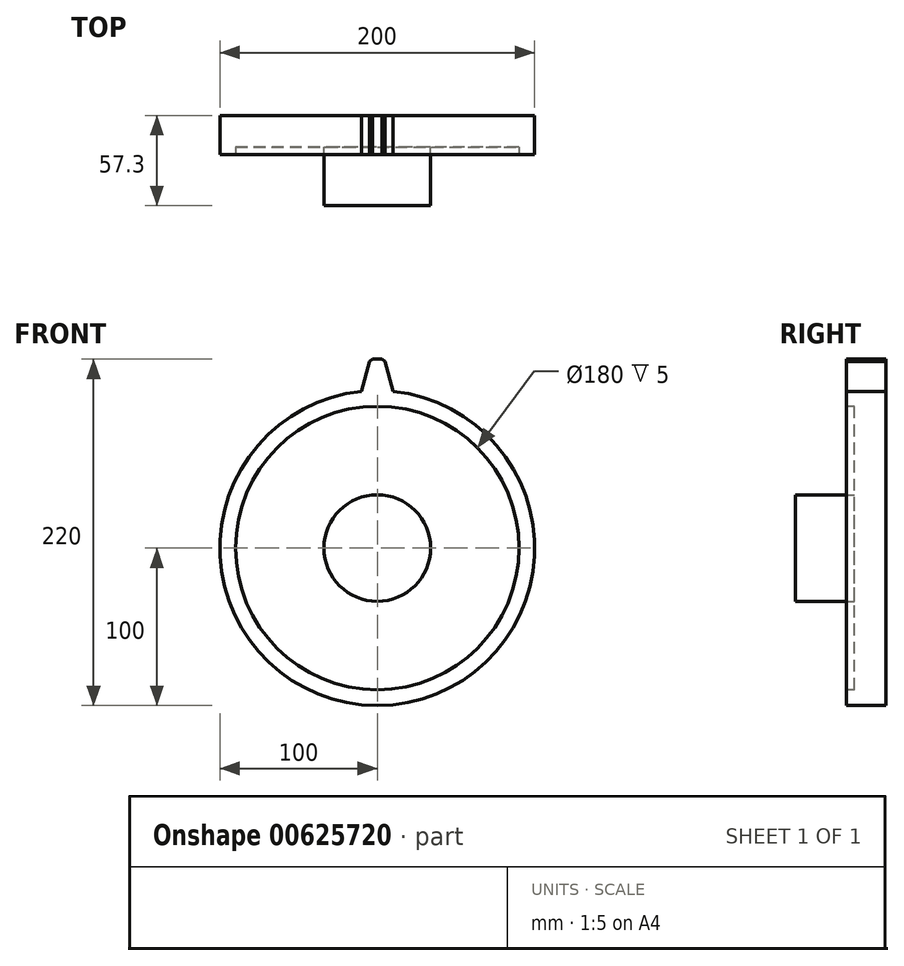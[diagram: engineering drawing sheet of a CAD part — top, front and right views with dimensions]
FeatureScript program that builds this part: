
annotation { "Feature Type Name" : "Feature", "Feature Type Description" : "" }
export const myFeature = defineFeature(function(context is Context, id is Id, definition is map)
    precondition{}
    {
        {
            var Q0;
            Q0=qCreatedBy(makeId("Front.planeOp"),FACE);
            var sketch = newSketch(context, id + "F0", { "sketchPlane" : qUnion([Q0])});
            skCircle(sketch, "E0", {"center": v(0, 0) * mm, "radius": 100 * mm});
            skSolve(sketch);
        }
        {
            var Q0;
            Q0 = qSketchRegion(id + "F0", true);
            extrude(context, id + "F1", {"entities" : qUnion([Q0]), "depth" : 25 * mm, "offsetDistance" : 25 * mm});
        }
        {
            var Q0;
            Q0=qCreatedBy(makeId("Front.planeOp"),FACE);
            var sketch = newSketch(context, id + "F2", { "sketchPlane" : qUnion([Q0])});
            skLineSegment(sketch, "E1", {"start": v(-10, 99.5) * mm, "end": v(10, 99.5) * mm});
            skLineSegment(sketch, "E2", {"start": v(10, 99.5) * mm, "end": v(4.5, 120) * mm});
            skLineSegment(sketch, "E3", {"start": v(4.5, 120) * mm, "end": v(-4.5, 120) * mm});
            skLineSegment(sketch, "E4", {"start": v(-4.5, 120) * mm, "end": v(-10, 99.5) * mm});
            skSolve(sketch);
        }
        {
            var Q0;
            Q0 = qSketchRegion(id + "F2", true);
            extrude(context, id + "F3", {"entities" : qUnion([Q0]), "operationType" : NewBodyOperationType.ADD, "depth" : 25 * mm, "offsetDistance" : 25 * mm});
        }
        {
            var Q0;
            Q0=makeQuery(id+"F3.opExtrude","SWEPT_EDGE",EDGE,{"disambiguationData":[OSD([sQuery(id+"F2.wireOp",EDGE,"E2"),sQuery(id+"F2.wireOp",EDGE,"E3")])]});
            var Q1;
            Q1=makeQuery(id+"F3.opExtrude","SWEPT_EDGE",EDGE,{"disambiguationData":[OSD([sQuery(id+"F2.wireOp",EDGE,"E3"),sQuery(id+"F2.wireOp",EDGE,"E4")])]});
            chamfer(context, id + "F4", {"entities" : qUnion([Q0, Q1]), "width" : 2 * mm, "tangentPropagation" : true});
        }
        {
            var Q0;
            Q0=makeQuery(id+"F3.opExtrude","SWEPT_EDGE",EDGE,{"disambiguationData":[OSD([sQuery(id+"F2.wireOp",EDGE,"E1"),sQuery(id+"F2.wireOp",EDGE,"E4")])]});
            var Q1;
            Q1=makeQuery(id+"F3.opExtrude","SWEPT_EDGE",EDGE,{"disambiguationData":[OSD([sQuery(id+"F2.wireOp",EDGE,"E1"),sQuery(id+"F2.wireOp",EDGE,"E2")])]});
            fillet(context, id + "F5", {"entities" : qUnion([Q0, Q1]), "radius" : 5 * mm, "tangentPropagation" : true, "allowEdgeOverflow" : false});
        }
        {
            var Q0;
            {var subQ0=sQuery(id+"F2.wireOp",EDGE,"E4");var subQ1=sQuery(id+"F2.wireOp",EDGE,"E3");var subQ2=sQuery(id+"F2.wireOp",EDGE,"E2");var subQ3=sQuery(id+"F2.wireOp",EDGE,"E1");Q0=makeQuery(id+"FSANccO2QEkQk0R_1.19.F3.boolean.opBoolean","MERGE",FACE,{"derivedFrom":[makeQuery(id+"FSANccO2QEkQk0R_1.18.F3.boolean.opBoolean","MERGE",FACE,{"derivedFrom":[makeQuery(id+"FSANccO2QEkQk0R_1.17.F3.boolean.opBoolean","MERGE",FACE,{"derivedFrom":[makeQuery(id+"FSANccO2QEkQk0R_1.16.F3.boolean.opBoolean","MERGE",FACE,{"derivedFrom":[makeQuery(id+"FSANccO2QEkQk0R_1.15.F3.boolean.opBoolean","MERGE",FACE,{"derivedFrom":[makeQuery(id+"FSANccO2QEkQk0R_1.14.F3.boolean.opBoolean","MERGE",FACE,{"derivedFrom":[makeQuery(id+"FSANccO2QEkQk0R_1.13.F3.boolean.opBoolean","MERGE",FACE,{"derivedFrom":[makeQuery(id+"FSANccO2QEkQk0R_1.12.F3.boolean.opBoolean","MERGE",FACE,{"derivedFrom":[makeQuery(id+"FSANccO2QEkQk0R_1.11.F3.boolean.opBoolean","MERGE",FACE,{"derivedFrom":[makeQuery(id+"FSANccO2QEkQk0R_1.10.F3.boolean.opBoolean","MERGE",FACE,{"derivedFrom":[makeQuery(id+"FSANccO2QEkQk0R_1.9.F3.boolean.opBoolean","MERGE",FACE,{"derivedFrom":[makeQuery(id+"FSANccO2QEkQk0R_1.8.F3.boolean.opBoolean","MERGE",FACE,{"derivedFrom":[makeQuery(id+"FSANccO2QEkQk0R_1.7.F3.boolean.opBoolean","MERGE",FACE,{"derivedFrom":[makeQuery(id+"FSANccO2QEkQk0R_1.6.F3.boolean.opBoolean","MERGE",FACE,{"derivedFrom":[makeQuery(id+"FSANccO2QEkQk0R_1.5.F3.boolean.opBoolean","MERGE",FACE,{"derivedFrom":[makeQuery(id+"FSANccO2QEkQk0R_1.4.F3.boolean.opBoolean","MERGE",FACE,{"derivedFrom":[makeQuery(id+"FSANccO2QEkQk0R_1.3.F3.boolean.opBoolean","MERGE",FACE,{"derivedFrom":[makeQuery(id+"FSANccO2QEkQk0R_1.2.F3.boolean.opBoolean","MERGE",FACE,{"derivedFrom":[makeQuery(id+"FSANccO2QEkQk0R_1.1.F3.boolean.opBoolean","MERGE",FACE,{"derivedFrom":[makeQuery(id+"F3.boolean.opBoolean","MERGE",FACE,{"derivedFrom":[makeQuery(id+"F1.opExtrude","CAP_FACE",FACE,{"disambiguationData":[OSD([sQuery(id+"F0.wireOp",EDGE,"E0")])],"isStart":false}),makeQuery(id+"F3.opExtrude","CAP_FACE",FACE,{"disambiguationData":[OSD([subQ3,subQ2,subQ1,subQ0])],"isStart":false})]}),makeQuery(id+"FSANccO2QEkQk0R_1.1.F3.opExtrude","CAP_FACE",FACE,{"disambiguationData":[OSD([subQ3,subQ2,subQ1,subQ0])],"isStart":false})]}),makeQuery(id+"FSANccO2QEkQk0R_1.2.F3.opExtrude","CAP_FACE",FACE,{"disambiguationData":[OSD([subQ3,subQ2,subQ1,subQ0])],"isStart":false})]}),makeQuery(id+"FSANccO2QEkQk0R_1.3.F3.opExtrude","CAP_FACE",FACE,{"disambiguationData":[OSD([subQ3,subQ2,subQ1,subQ0])],"isStart":false})]}),makeQuery(id+"FSANccO2QEkQk0R_1.4.F3.opExtrude","CAP_FACE",FACE,{"disambiguationData":[OSD([subQ3,subQ2,subQ1,subQ0])],"isStart":false})]}),makeQuery(id+"FSANccO2QEkQk0R_1.5.F3.opExtrude","CAP_FACE",FACE,{"disambiguationData":[OSD([subQ3,subQ2,subQ1,subQ0])],"isStart":false})]}),makeQuery(id+"FSANccO2QEkQk0R_1.6.F3.opExtrude","CAP_FACE",FACE,{"disambiguationData":[OSD([subQ3,subQ2,subQ1,subQ0])],"isStart":false})]}),makeQuery(id+"FSANccO2QEkQk0R_1.7.F3.opExtrude","CAP_FACE",FACE,{"disambiguationData":[OSD([subQ3,subQ2,subQ1,subQ0])],"isStart":false})]}),makeQuery(id+"FSANccO2QEkQk0R_1.8.F3.opExtrude","CAP_FACE",FACE,{"disambiguationData":[OSD([subQ3,subQ2,subQ1,subQ0])],"isStart":false})]}),makeQuery(id+"FSANccO2QEkQk0R_1.9.F3.opExtrude","CAP_FACE",FACE,{"disambiguationData":[OSD([subQ3,subQ2,subQ1,subQ0])],"isStart":false})]}),makeQuery(id+"FSANccO2QEkQk0R_1.10.F3.opExtrude","CAP_FACE",FACE,{"disambiguationData":[OSD([subQ3,subQ2,subQ1,subQ0])],"isStart":false})]}),makeQuery(id+"FSANccO2QEkQk0R_1.11.F3.opExtrude","CAP_FACE",FACE,{"disambiguationData":[OSD([subQ3,subQ2,subQ1,subQ0])],"isStart":false})]}),makeQuery(id+"FSANccO2QEkQk0R_1.12.F3.opExtrude","CAP_FACE",FACE,{"disambiguationData":[OSD([subQ3,subQ2,subQ1,subQ0])],"isStart":false})]}),makeQuery(id+"FSANccO2QEkQk0R_1.13.F3.opExtrude","CAP_FACE",FACE,{"disambiguationData":[OSD([subQ3,subQ2,subQ1,subQ0])],"isStart":false})]}),makeQuery(id+"FSANccO2QEkQk0R_1.14.F3.opExtrude","CAP_FACE",FACE,{"disambiguationData":[OSD([subQ3,subQ2,subQ1,subQ0])],"isStart":false})]}),makeQuery(id+"FSANccO2QEkQk0R_1.15.F3.opExtrude","CAP_FACE",FACE,{"disambiguationData":[OSD([subQ3,subQ2,subQ1,subQ0])],"isStart":false})]}),makeQuery(id+"FSANccO2QEkQk0R_1.16.F3.opExtrude","CAP_FACE",FACE,{"disambiguationData":[OSD([subQ3,subQ2,subQ1,subQ0])],"isStart":false})]}),makeQuery(id+"FSANccO2QEkQk0R_1.17.F3.opExtrude","CAP_FACE",FACE,{"disambiguationData":[OSD([subQ3,subQ2,subQ1,subQ0])],"isStart":false})]}),makeQuery(id+"FSANccO2QEkQk0R_1.18.F3.opExtrude","CAP_FACE",FACE,{"disambiguationData":[OSD([subQ3,subQ2,subQ1,subQ0])],"isStart":false})]}),makeQuery(id+"FSANccO2QEkQk0R_1.19.F3.opExtrude","CAP_FACE",FACE,{"disambiguationData":[OSD([subQ3,subQ2,subQ1,subQ0])],"isStart":false})]});}
            var sketch = newSketch(context, id + "F6", { "sketchPlane" : qUnion([Q0])});
            skCircle(sketch, "E5", {"center": v(0, 0) * mm, "radius": 90 * mm});
            skSolve(sketch);
        }
        {
            var Q0;
            Q0=makeQuery(id+"F6.imprint","IMPRINT",FACE,{"disambiguationData":[TD([[makeQuery(id+"F6.imprint","IMPRINT",EDGE,{"derivedFrom":sQuery(id+"F6.wireOp",EDGE,"E5")}),1.0]])]});
            extrude(context, id + "F7", {"entities" : qUnion([Q0]), "operationType" : NewBodyOperationType.ADD, "depth" : 5 * mm, "offsetDistance" : 25 * mm});
        }
        {
            var Q0;
            Q0=makeQuery(id+"F7.opExtrude","CAP_FACE",FACE,{"disambiguationData":[OSD([sQuery(id+"F6.wireOp",EDGE,"E5")])],"isStart":false});
            extrude(context, id + "F8", {"entities" : qUnion([Q0]), "operationType" : NewBodyOperationType.ADD, "depth" : 5 * mm, "offsetDistance" : 25 * mm});
        }
        {
            var Q0;
            Q0=makeQuery(id+"F8.opExtrude","CAP_FACE",FACE,{"disambiguationData":[OSD([sQuery(id+"F6.wireOp",EDGE,"E5")])],"isStart":false});
            extrude(context, id + "F9", {"entities" : qUnion([Q0]), "operationType" : NewBodyOperationType.REMOVE, "oppositeDirection" : true, "depth" : 5 * mm, "offsetDistance" : 25 * mm});
        }
        {
            var Q0;
            Q0=makeQuery(id+"F9.boolean.opBoolean","COPY",FACE,{"derivedFrom":makeQuery(id+"F9.opExtrude","CAP_FACE",FACE,{"disambiguationData":[OSD([sQuery(id+"F6.wireOp",EDGE,"E5")])],"isStart":false})});
            extrude(context, id + "F10", {"entities" : qUnion([Q0]), "operationType" : NewBodyOperationType.REMOVE, "oppositeDirection" : true, "depth" : 10 * mm, "offsetDistance" : 25 * mm});
        }
        {
            var Q0;
            Q0=makeQuery(id+"F10.boolean.opBoolean","COPY",FACE,{"derivedFrom":makeQuery(id+"F10.opExtrude","CAP_FACE",FACE,{"disambiguationData":[OSD([sQuery(id+"F6.wireOp",EDGE,"E5")])],"isStart":false})});
            var sketch = newSketch(context, id + "F11", { "sketchPlane" : qUnion([Q0])});
            skCircle(sketch, "E6", {"center": v(0, 0) * mm, "radius": 33.86 * mm});
            skSolve(sketch);
        }
        {
            var Q0;
            Q0=makeQuery(id+"F11.imprint","IMPRINT",FACE,{"disambiguationData":[TD([[makeQuery(id+"F11.imprint","IMPRINT",EDGE,{"derivedFrom":sQuery(id+"F11.wireOp",EDGE,"E6")}),1.0]])]});
            extrude(context, id + "F12", {"entities" : qUnion([Q0]), "operationType" : NewBodyOperationType.ADD, "depth" : 37.3 * mm, "offsetDistance" : 25 * mm});
        }
    });
